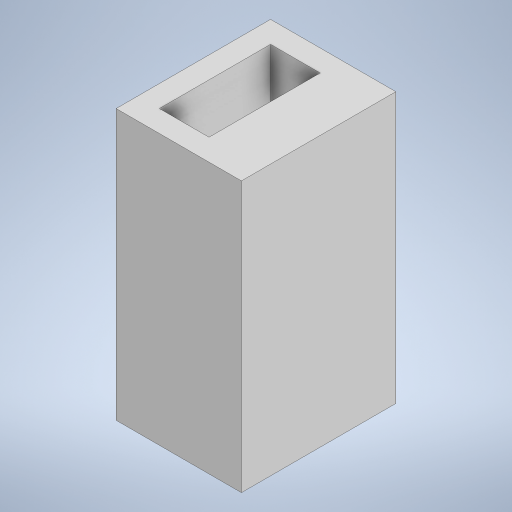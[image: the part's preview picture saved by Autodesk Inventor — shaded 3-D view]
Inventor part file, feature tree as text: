
AUTODESK INVENTOR PART (.ipt)
format: ipt  version: 2023 (Build 270158000, 158)  size: 206,848 bytes
history: native  units: mm
features: extrude x2, sketch x2, other x1
ambient origin geometry x8: Origin, YZ Plane, XZ Plane, XY Plane, X Axis, Y Axis, Z Axis, Center Point
bodies: Body1 (feature_tree)
feature tree (5):
  other  "Sólido1"
  extrude  "Extrusión1"  Depth=4.6mm
  extrude  "Extrusión2"  Depth=2.0mm TaperAngle=0.0deg
  sketch  "Boceto1"  dims[d0=10.3mm d1=4.6mm]
  sketch  "Boceto3"  dims[d2=2.0mm d3=2.0mm d4=0.0mm d5=2.0mm d6=5.0mm d7=25.0mm d8=0.0mm]
